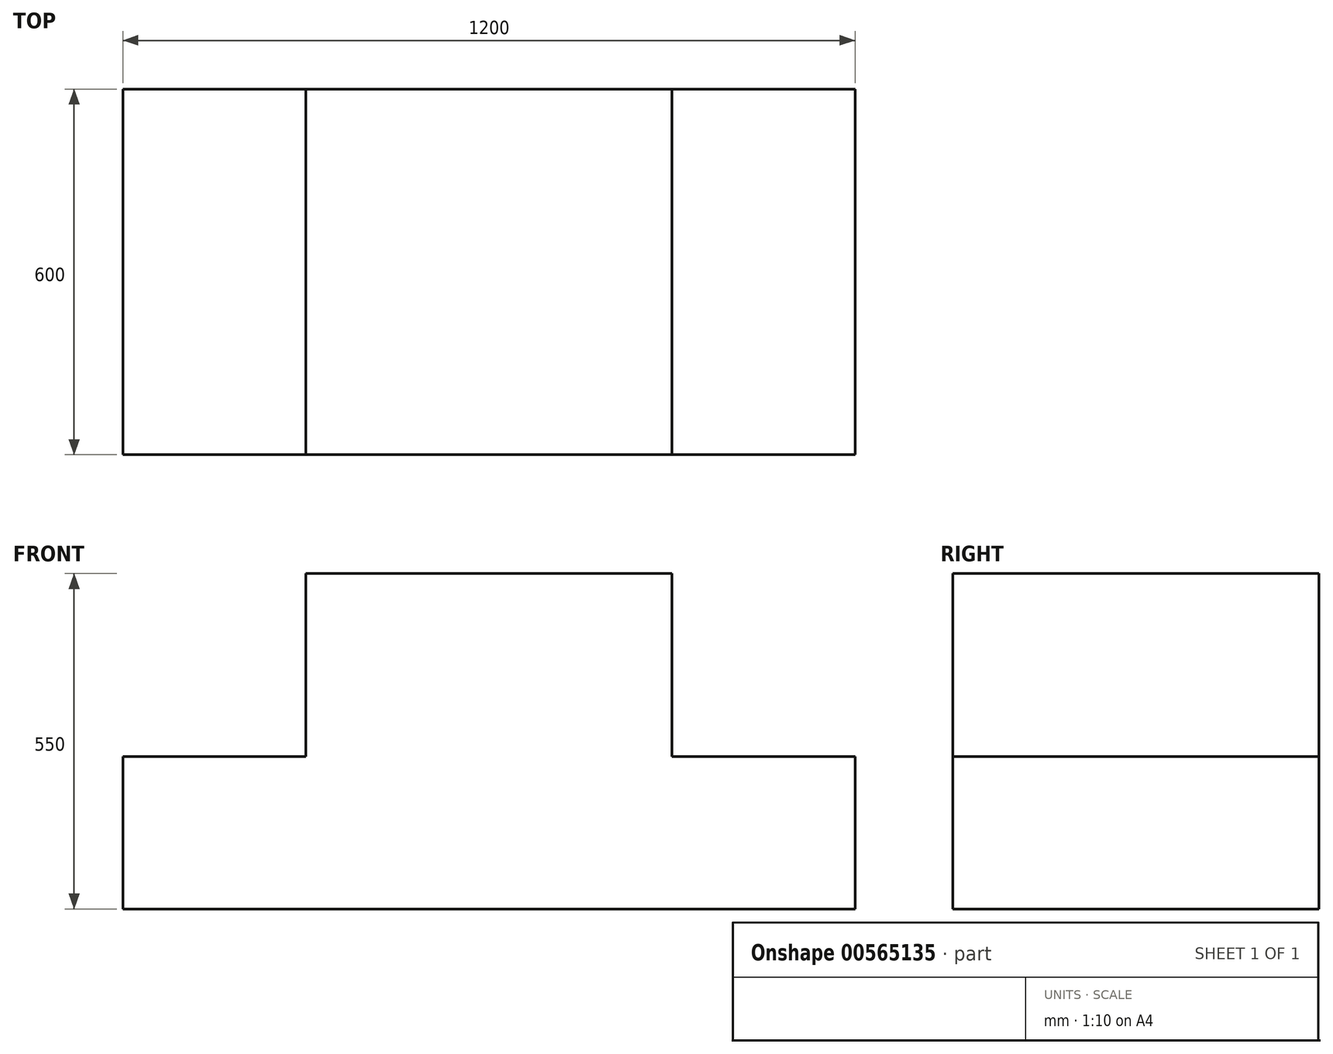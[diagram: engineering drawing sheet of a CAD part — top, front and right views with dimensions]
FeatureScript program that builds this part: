
annotation { "Feature Type Name" : "Feature", "Feature Type Description" : "" }
export const myFeature = defineFeature(function(context is Context, id is Id, definition is map)
    precondition{}
    {
        {
            var Q0;
            Q0=qCreatedBy(makeId("Front.planeOp"),FACE);
            var sketch = newSketch(context, id + "F0", { "sketchPlane" : qUnion([Q0])});
            skLineSegment(sketch, "E0.bottom", {"start": v(300, 275) * mm, "end": v(-300, 275) * mm});
            skLineSegment(sketch, "E0.top", {"start": v(600, -275) * mm, "end": v(-600, -275) * mm});
            skLineSegment(sketch, "E0.left", {"start": v(600, -25) * mm, "end": v(600, -275) * mm});
            skLineSegment(sketch, "E0.right", {"start": v(-600, -25) * mm, "end": v(-600, -275) * mm});
            skPoint(sketch, "E0.middle", {"position": v(0, 0) * mm});
            skLineSegment(sketch, "E1", {"start": v(-600, -25) * mm, "end": v(-300, -25) * mm});
            skLineSegment(sketch, "E2", {"start": v(-300, -25) * mm, "end": v(-300, 275) * mm});
            skLineSegment(sketch, "E3", {"start": v(-300, 275) * mm, "end": v(300, 275) * mm});
            skLineSegment(sketch, "E4", {"start": v(300, 275) * mm, "end": v(300, -25) * mm});
            skLineSegment(sketch, "E5", {"start": v(300, -25) * mm, "end": v(600, -25) * mm});
            skPoint(sketch, "E6.orphan", {"position": v(600, 275) * mm});
            skPoint(sketch, "E7.orphan", {"position": v(-600, 275) * mm});
            skSolve(sketch);
        }
        {
            var Q0;
            Q0 = qSketchRegion(id + "F0", true);
            extrude(context, id + "F1", {"entities" : qUnion([Q0]), "depth" : 600 * mm, "offsetDistance" : 25.4 * mm});
        }
        {
            var Q0;
            Q0 = qSketchRegion(id + "F0", true);
            extrude(context, id + "F2", {"entities" : qUnion([Q0]), "operationType" : NewBodyOperationType.ADD, "depth" : 600 * mm, "offsetDistance" : 25.4 * mm});
        }
    });
